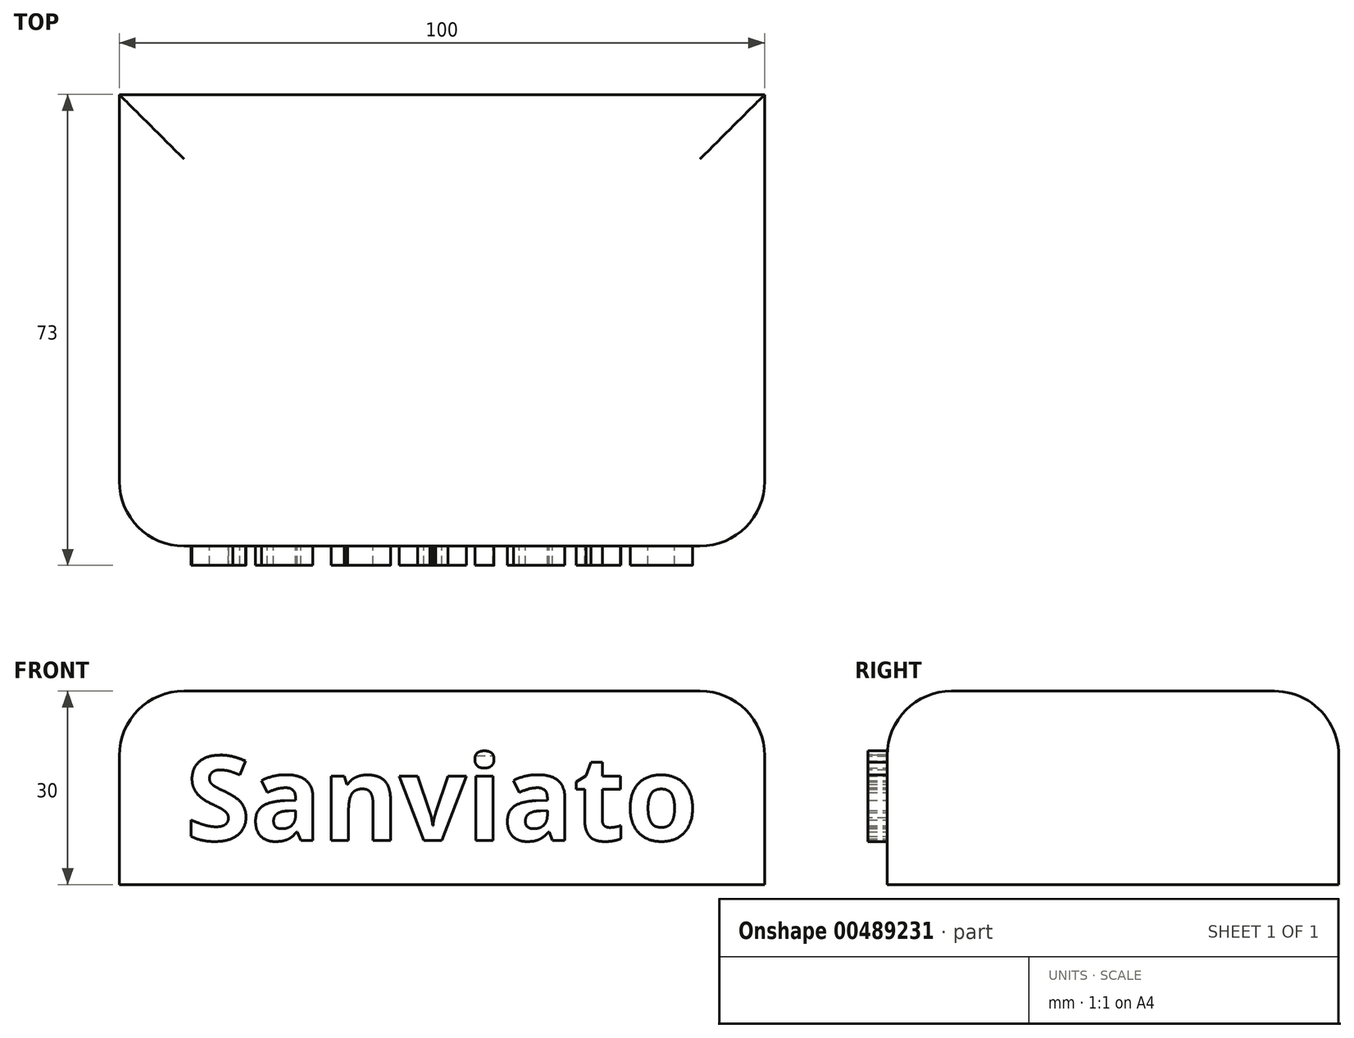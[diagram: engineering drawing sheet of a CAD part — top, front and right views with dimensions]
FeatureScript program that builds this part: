
annotation { "Feature Type Name" : "Feature", "Feature Type Description" : "" }
export const myFeature = defineFeature(function(context is Context, id is Id, definition is map)
    precondition{}
    {
        {
            var Q0;
            Q0=qCreatedBy(makeId("Top.planeOp"),FACE);
            var sketch = newSketch(context, id + "F0", { "sketchPlane" : qUnion([Q0])});
            skLineSegment(sketch, "E0", {"start": v(-50.74, 46.04) * mm, "end": v(-50.74, -23.96) * mm});
            skLineSegment(sketch, "E1", {"start": v(-50.74, -23.96) * mm, "end": v(49.26, -23.96) * mm});
            skLineSegment(sketch, "E2", {"start": v(49.26, -23.96) * mm, "end": v(49.26, 46.04) * mm});
            skLineSegment(sketch, "E3", {"start": v(49.26, 46.04) * mm, "end": v(-50.74, 46.04) * mm});
            skSolve(sketch);
        }
        {
            var Q0;
            Q0=makeQuery(id+"F0.imprint","IMPRINT",FACE,{"disambiguationData":[TD([[makeQuery(id+"F0.imprint","IMPRINT",EDGE,{"derivedFrom":sQuery(id+"F0.wireOp",EDGE,"E0")}),1.0]])]});
            extrude(context, id + "F1", {"entities" : qUnion([Q0]), "depth" : 30 * mm});
        }
        {
            var Q0;
            Q0=makeQuery(id+"F1.opExtrude","CAP_EDGE",EDGE,{"disambiguationData":[OSD([sQuery(id+"F0.wireOp",EDGE,"E1")])],"isStart":false});
            fillet(context, id + "F2", {"entities" : qUnion([Q0]), "radius" : 10 * mm, "tangentPropagation" : true, "allowEdgeOverflow" : false});
        }
        {
            var Q0;
            Q0=makeQuery(id+"F1.opExtrude","CAP_EDGE",EDGE,{"disambiguationData":[OSD([sQuery(id+"F0.wireOp",EDGE,"E2")])],"isStart":false});
            var Q1;
            Q1=makeQuery(id+"F1.opExtrude","CAP_EDGE",EDGE,{"disambiguationData":[OSD([sQuery(id+"F0.wireOp",EDGE,"E0")])],"isStart":false});
            var Q2;
            Q2=makeQuery(id+"F1.opExtrude","CAP_EDGE",EDGE,{"disambiguationData":[OSD([sQuery(id+"F0.wireOp",EDGE,"E3")])],"isStart":false});
            fillet(context, id + "F3", {"entities" : qUnion([Q0, Q1, Q2]), "radius" : 10 * mm, "tangentPropagation" : true, "allowEdgeOverflow" : false});
        }
        {
            var Q0;
            Q0=makeQuery(id+"F1.opExtrude","SWEPT_FACE",FACE,{"disambiguationData":[OSD([sQuery(id+"F0.wireOp",EDGE,"E1")])]});
            var sketch = newSketch(context, id + "F4", { "sketchPlane" : qUnion([Q0])});
            skText(sketch, "E4", { "text": "Sanviato", "fontName": "OpenSans-Bold.ttf"});
            const initialGuessF4  = {"E4": [-0.04047, 0.00684, 1, 0, 0.01316]};
            skSetInitialGuess(sketch, initialGuessF4);
            skSolve(sketch);
        }
        {
            var Q0;
            Q0 = qSketchRegion(id + "F4", true);
            extrude(context, id + "F5", {"entities" : qUnion([Q0]), "operationType" : NewBodyOperationType.ADD, "depth" : 3 * mm});
        }
    });
